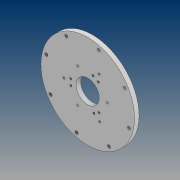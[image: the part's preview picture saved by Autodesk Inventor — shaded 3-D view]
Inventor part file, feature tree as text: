
AUTODESK INVENTOR PART (.ipt)
format: ipt  version: 2021 (Build 250183000, 183)  size: 2,050,560 bytes
history: native  units: mm
features: thread x25, sketch x9, extrude x9, pattern_circular x5, revolve x1
ambient origin geometry x8: Origin, YZ Plane, XZ Plane, XY Plane, X Axis, Y Axis, Z Axis, Center Point
bodies: Body1 (feature_tree)
feature tree (49):
  sketch  "Sketch2"  dims[d19=20.0mm]
  extrude  "Extrusion2"  Depth=30.0mm TaperAngle=360.0deg
  thread  "Thread1"  [1 undecoded]
  thread  "Thread2"  [1 undecoded]
  thread  "Thread3"  [1 undecoded]
  thread  "Thread4"  [1 undecoded]
  thread  "Thread5"  [1 undecoded]
  thread  "Thread6"  [1 undecoded]
  extrude  "Extrusion3"  Depth=20.0mm TaperAngle=0.0deg
  extrude  "Extrusion4"  Depth=20.0mm
  sketch  "Sketch4"  dims[d72=20.0mm d73=0.0mm d74=20.0mm d75=0.0mm]
  extrude  "Extrusion5"  Depth=30.0mm TaperAngle=360.0deg
  pattern_circular  "Circular Pattern1"  Count=23  [1 undecoded]
  extrude  "Extrusion7"  Depth=850.0mm
  extrude  "Extrusion8"  Depth=50.0mm TaperAngle=0.0deg
  revolve  "Revolution1"  [1 undecoded]
  pattern_circular  "Circular Pattern3"  [2 undecoded]
  extrude  "Extrusion9"  Depth=930.0mm
  pattern_circular  "Circular Pattern4"  [2 undecoded]
  extrude  "Extrusion10"  Depth=260.0mm
  pattern_circular  "Circular Pattern5"  [2 undecoded]
  thread  "Thread7"  [1 undecoded]
  thread  "Thread8"  [1 undecoded]
  thread  "Thread9"  [1 undecoded]
  thread  "Thread10"  [1 undecoded]
  thread  "Thread11"  [1 undecoded]
  thread  "Thread12"  [1 undecoded]
  thread  "Thread13"  [1 undecoded]
  thread  "Thread14"  [1 undecoded]
  thread  "Thread15"  [1 undecoded]
  thread  "Thread16"  [1 undecoded]
  thread  "Thread17"  [1 undecoded]
  thread  "Thread18"  [1 undecoded]
  thread  "Thread19"  [1 undecoded]
  thread  "Thread20"  [1 undecoded]
  pattern_circular  "Circular Pattern6"  [2 undecoded]
  thread  "Thread21"  [1 undecoded]
  thread  "Thread22"  [1 undecoded]
  thread  "Thread23"  [1 undecoded]
  thread  "Thread24"  [1 undecoded]
  thread  "Thread25"  [1 undecoded]
  extrude  "Extrusion11"  Depth=45.0mm TaperAngle=0.0deg
  sketch  "Sketch3"  dims[d43=30.0mm d44=470.0mm d45=20.0mm d46=20.0mm d47=170.0mm d48=20.0mm d49=3.490659mm d50=20.0mm d51=360.0deg d52=234.983926mm d53=30.0mm d55=360.0deg d57=30.0mm d59=360.0deg d61=930.0mm d62=20.0mm d63=0.0mm d64=20.0mm d65=0.0mm d66=20.0mm d67=0.0mm d68=20.0mm d69=0.0mm d70=20.0mm d71=0.0mm]
  sketch  "Sketch6"  dims[d76=392.0mm d84=20.0mm]
  sketch  "Sketch7"  dims[d89=0.0mm d90=0.0mm d92=30.0mm d94=360.0deg d96=230.0mm]
  sketch  "Sketch8"  dims[d97=10.0mm d98=0.0mm d99=850.0mm]
  sketch  "Sketch9"  dims[d101=80.0mm d103=360.0deg d105=50.0mm d106=0.0mm]
  sketch  "Sketch10"  dims[d107=80.0mm d108=360.0deg d112=111.6mm]
  sketch  "Sketch11"  dims[d113=0.0mm d114=0.0mm d123=930.0mm d124=25.0mm d125=0.0mm d126=260.0mm d127=16.0mm d132=15.0mm d133=0.0mm d134=90.0deg d135=50.0mm d136=360.0deg d138=0.0mm d139=0.0mm d140=30.0mm d141=360.0deg d143=0.0mm d144=0.0mm d145=80.0mm d146=360.0deg d148=45.0mm d149=0.0mm d150=45.0mm d151=0.0mm d152=45.0mm d153=0.0mm d154=45.0mm d155=0.0mm d156=45.0mm d157=0.0mm d158=45.0mm d159=0.0mm d160=45.0mm d161=0.0mm d162=45.0mm d163=0.0mm d164=45.0mm d165=0.0mm d166=45.0mm d167=0.0mm d168=45.0mm d169=0.0mm d170=45.0mm d171=0.0mm d172=45.0mm d173=0.0mm d174=45.0mm d175=0.0mm d176=45.0deg d177=135.0deg d178=90.0deg d179=50.0mm d180=360.0deg d182=50.0mm d184=360.0deg d186=15.0mm d187=0.0mm d188=15.0mm d189=0.0mm d190=15.0mm d191=0.0mm d192=15.0mm d193=0.0mm d194=15.0mm d195=0.0mm d196=1.0mm d197=0.0mm]
note: 35 required parameter values undecoded (feature->parameter linkage not recoverable at this tier; creation-order binding heuristic only, values carry confidence <= 0.55)